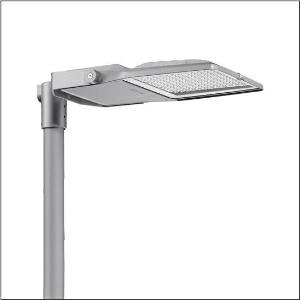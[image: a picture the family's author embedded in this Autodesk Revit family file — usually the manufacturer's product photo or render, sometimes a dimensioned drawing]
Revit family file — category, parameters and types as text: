
# Revit family: floodlight_fl_21_iq_midi___pl43_5xa7781f4a3a_cde7
name_source: partatom
category: Lighting Fixtures
units: mm (PartAtom-declared; Revit-internal decimal feet)

## family parameters
Cut with Voids When Loaded = No
Host = Face
Light Source = No
Part Type = Normal
Room Calculation Point = No
Round Connector Dimension = Use Diameter
Shared = No

## types (1)
- --- (1 x LED, 38290 lm, 270.2 W, 4000K)
    Apparent Load = 270 VA
    CIE Flux Codes = 27 78 99 100 100
    Color Rendering = 70
    Color Temperature = 4000K
    Default Elevation = 1800 mm
    Description = Floodlight FL 21 iQ midi, floodlight, primary light control with lens, of PMMA, primary optical cover: protective disc, of toughened safety glass, transparent, light distribution: PL43, light emission: direct distribution, installation type: surface-mounted, LED, High Power LED, rated luminous flux: 38.290lm, luminous efficacy: 142lm/W, light colour: 740, colour temperature: 4000K, control gear: ECG iQ, control: optimised constant luminous flux control (CLO 2.0), Desk-Remote (wireless, voltage-free reading and setting of iQ features in the workshop via application-optimized NFC function/RFID function), Light-Fading, Smart-Wire, Night-Set, Lumen-Switch, Temp-Guard, Auto-Match, with terminal, 6-pole, mains connection: 220..240V, AC, 50/60Hz, start of lifetime: 270W, end of service life: 287W, reduction: 118W, luminaire housing, of diecast aluminium, powder-coated, Siteco® metallic grey (DB 702S), corrosivity category C5 mid according to DIN EN ISO 12944, sealing non-destructively replaceable, please order mast flange separately, mast bracket, of steel, galvanised, powder-coated, Siteco® metallic grey (DB 702S), protection rating (complete): IP66, insulation class (complete): insulation class II (safety insulation), certification: CE, protection symbol: D, impact resistance: IK08, permissible operating ambient temperature: -40..+40°C, permissible operating ambient temperature for outdoor applications: -40..+50°C, standard: DIN EN 12944, LABS conformity tested according to VDMA 24364:2018-05, packaging unit: 1 piece

Light Distribution: PL43
    Height = 76 mm
    Lamp = 1 x LED
    Lamp Light Flux = 38290 lm
    Lamp Power = 270.2 W
    Lamp count = 1
    Length = 657 mm
    Luminous efficacy = 142 lm/W
    Manufacturer = Siteco
    ModVariant = No
    Model = 5XA7781F4A3A
    Number of Poles = 1
    OnlyDefault = Yes
    Power Factor = 1
    Product Name = Floodlight FL 21 iQ midi | PL43
    Product group = floodlight | pylon annexe
    ProductGroupID = 6200
    Protection Class = Protection class II
    Protection Degree = IP 66
    RLX_Detail_Level = 1
    RLX_Emergency_Light_Flux = 0 lm
    RLX_Emergency_Type = 0
    RLX_Emergency_Type_DB = No
    RlxData = <blob elided: 153569 chars, md5=7b5fdf9b>
    Socket = socket
    Standby Power = 0 W
    System Light Flux = 38290 lm
    System Power = 270 W
    Type Comments = factory setting: luminous flux: 100 % | dim-lin: 254 | 620 mA
    Type Image = l_1007123.jpg
    URL = http://relux.com
    VarID = @adj_053097
    Voltage = 0 V
    Weight = 0.00 kg
    Width = 442 mm

## geometry (parser evidence)
native form markers: Blend x4, Sweep x14
no freeform markers — native parametric forms only
